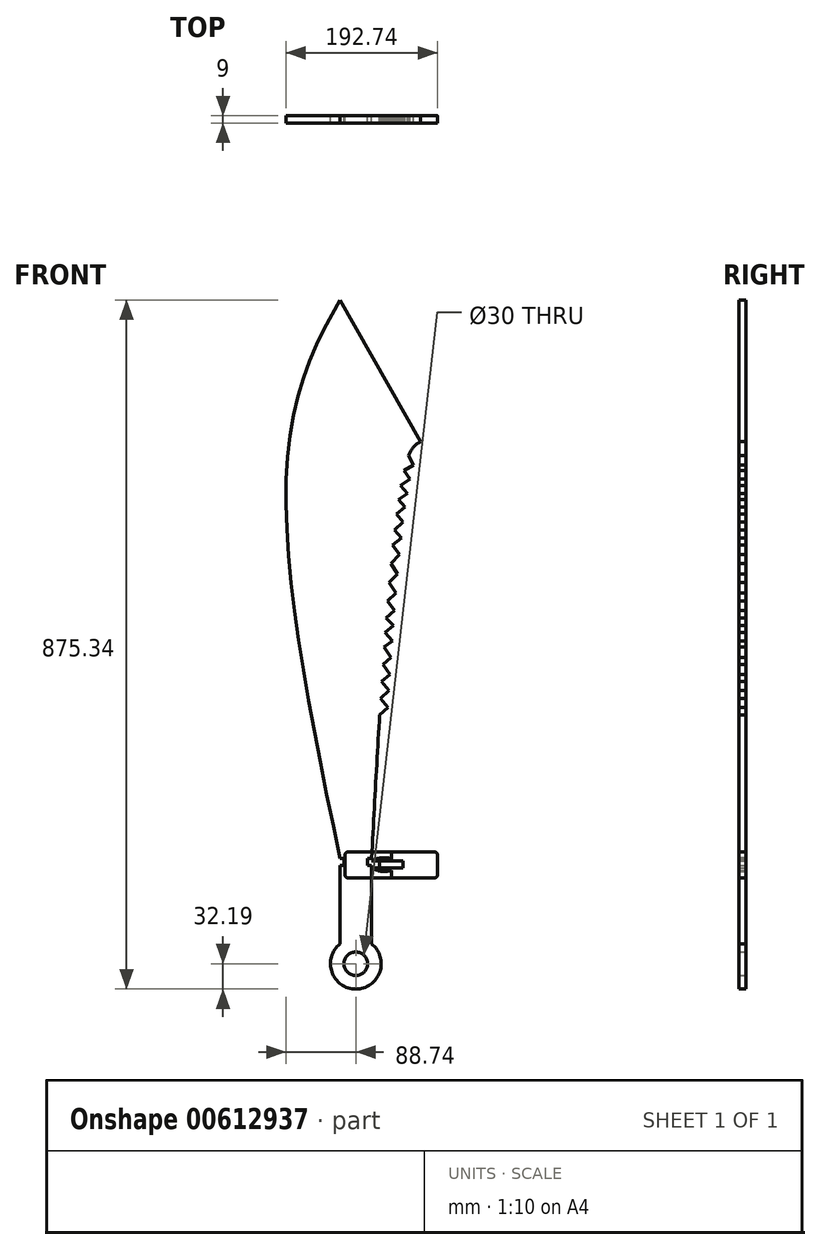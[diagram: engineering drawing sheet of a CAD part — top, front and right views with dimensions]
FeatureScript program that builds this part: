
annotation { "Feature Type Name" : "Feature", "Feature Type Description" : "" }
export const myFeature = defineFeature(function(context is Context, id is Id, definition is map)
    precondition{}
    {
        {
            var Q0;
            Q0=qCreatedBy(makeId("Front.planeOp"),FACE);
            var sketch = newSketch(context, id + "F0", { "sketchPlane" : qUnion([Q0])});
            skLineSegment(sketch, "E0.top", {"start": v(20, 49.92) * mm, "end": v(-20, 49.92) * mm});
            skLineSegment(sketch, "E0.left", {"start": v(20, -49.92) * mm, "end": v(20, 49.92) * mm});
            skLineSegment(sketch, "E0.right", {"start": v(-20, -49.92) * mm, "end": v(-20, 49.92) * mm});
            skPoint(sketch, "E0.middle", {"position": v(0, 0) * mm});
            skLineSegment(sketch, "E1", {"start": v(20, 49.92) * mm, "end": v(15, 49.92) * mm, "construction": true});
            skLineSegment(sketch, "E2", {"start": v(-20, 49.92) * mm, "end": v(-15, 49.92) * mm, "construction": true});
            skLineSegment(sketch, "E3", {"start": v(-15, 49.92) * mm, "end": v(-15, 58.92) * mm, "construction": true});
            skLineSegment(sketch, "E4", {"start": v(15, 58.92) * mm, "end": v(15, 49.92) * mm, "construction": true});
            skFitSpline(sketch, "E5", {"points": [v(20, 58.92) * mm, v(66.96, 570.52) * mm, v(82.11, 588.05) * mm], "startDerivative": vector(45.15, 820.54) * mm, "endDerivative": vector(88.4, 54.26) * mm});
            skLineSegment(sketch, "E6", {"start": v(82.11, 588.05) * mm, "end": v(-20, 768) * mm});
            skFitSpline(sketch, "E7", {"points": [v(-20, 58.92) * mm, v(-86.64, 570.52) * mm, v(-20, 768) * mm, v(22.37, 827.27) * mm], "startDerivative": vector(-243.66, 1152.7) * mm, "endDerivative": vector(43.6, -18.4) * mm});
            skLineSegment(sketch, "E8", {"start": v(20, 58.92) * mm, "end": v(15, 58.92) * mm});
            skLineSegment(sketch, "E9", {"start": v(15, 49.92) * mm, "end": v(15, 58.92) * mm});
            skLineSegment(sketch, "E10", {"start": v(-20, 58.92) * mm, "end": v(-15, 58.92) * mm});
            skLineSegment(sketch, "E11", {"start": v(-15, 49.92) * mm, "end": v(-15, 58.92) * mm});
            skPoint(sketch, "E12.visualSharp", {"position": v(20, -49.92) * mm});
            skLineSegment(sketch, "E12.filletArc", {"start": v(20, -49.92) * mm, "end": v(20, -49.92) * mm});
            skPoint(sketch, "E13.visualSharp", {"position": v(-20, -49.92) * mm});
            skLineSegment(sketch, "E13.filletArc", {"start": v(-20, -49.92) * mm, "end": v(-20, -49.92) * mm});
            skLineSegment(sketch, "E14", {"start": v(0, -49.92) * mm, "end": v(0, -75.15) * mm, "construction": true});
            skArc(sketch, "E15", {"start": v(-20, -49.92) * mm, "mid": v(0, -107.34) * mm, "end": v(20, -49.92) * mm});
            skCircle(sketch, "E16", {"center": v(0, -75.15) * mm, "radius": 15 * mm});
            skLineSegment(sketch, "E17", {"start": v(66.96, 570.52) * mm, "end": v(73.2, 558.15) * mm});
            skLineSegment(sketch, "E18", {"start": v(73.2, 558.15) * mm, "end": v(61, 551.35) * mm});
            skLineSegment(sketch, "E19", {"start": v(61, 551.35) * mm, "end": v(68.86, 540.72) * mm});
            skLineSegment(sketch, "E20", {"start": v(68.86, 540.72) * mm, "end": v(56.98, 532.25) * mm});
            skLineSegment(sketch, "E21", {"start": v(56.98, 532.25) * mm, "end": v(65.4, 522.25) * mm});
            skLineSegment(sketch, "E22", {"start": v(65.4, 522.25) * mm, "end": v(54, 514.42) * mm});
            skLineSegment(sketch, "E23", {"start": v(54, 514.42) * mm, "end": v(62.69, 504.73) * mm});
            skLineSegment(sketch, "E24", {"start": v(62.69, 504.73) * mm, "end": v(51.36, 495.86) * mm});
            skLineSegment(sketch, "E25", {"start": v(51.36, 495.86) * mm, "end": v(60.17, 485.9) * mm});
            skLineSegment(sketch, "E26", {"start": v(60.17, 485.9) * mm, "end": v(48.87, 475.9) * mm});
            skLineSegment(sketch, "E27", {"start": v(48.87, 475.9) * mm, "end": v(57.81, 465.9) * mm});
            skLineSegment(sketch, "E28", {"start": v(57.81, 465.9) * mm, "end": v(46.77, 457) * mm});
            skLineSegment(sketch, "E29", {"start": v(46.77, 457) * mm, "end": v(55.57, 444.65) * mm});
            skLineSegment(sketch, "E30", {"start": v(55.57, 444.65) * mm, "end": v(44.4, 433.34) * mm});
            skLineSegment(sketch, "E31", {"start": v(44.4, 433.34) * mm, "end": v(53.18, 419.7) * mm});
            skLineSegment(sketch, "E32", {"start": v(53.18, 419.7) * mm, "end": v(42.21, 409.4) * mm});
            skLineSegment(sketch, "E33", {"start": v(42.21, 409.4) * mm, "end": v(51.12, 396.02) * mm});
            skLineSegment(sketch, "E34", {"start": v(51.12, 396.02) * mm, "end": v(40.2, 385.4) * mm});
            skLineSegment(sketch, "E35", {"start": v(40.2, 385.4) * mm, "end": v(49.33, 373.87) * mm});
            skLineSegment(sketch, "E36", {"start": v(49.33, 373.87) * mm, "end": v(38.53, 364.07) * mm});
            skLineSegment(sketch, "E37", {"start": v(38.53, 364.07) * mm, "end": v(47.85, 354.5) * mm});
            skLineSegment(sketch, "E38", {"start": v(47.85, 354.5) * mm, "end": v(37.18, 345.88) * mm});
            skLineSegment(sketch, "E39", {"start": v(37.18, 345.88) * mm, "end": v(46.42, 334.84) * mm});
            skLineSegment(sketch, "E40", {"start": v(46.42, 334.84) * mm, "end": v(35.85, 327.14) * mm});
            skLineSegment(sketch, "E41", {"start": v(35.85, 327.14) * mm, "end": v(44.97, 313.9) * mm});
            skLineSegment(sketch, "E42", {"start": v(44.97, 313.9) * mm, "end": v(34.35, 305.24) * mm});
            skLineSegment(sketch, "E43", {"start": v(34.35, 305.24) * mm, "end": v(43.53, 292.29) * mm});
            skLineSegment(sketch, "E44", {"start": v(43.53, 292.29) * mm, "end": v(32.92, 283.37) * mm});
            skLineSegment(sketch, "E45", {"start": v(32.92, 283.37) * mm, "end": v(42.23, 272.02) * mm});
            skLineSegment(sketch, "E46", {"start": v(42.23, 272.02) * mm, "end": v(31.57, 262.05) * mm});
            skLineSegment(sketch, "E47", {"start": v(31.57, 262.05) * mm, "end": v(40.9, 250.72) * mm});
            skLineSegment(sketch, "E48", {"start": v(40.9, 250.72) * mm, "end": v(30.27, 240.75) * mm});
            skFitSpline(sketch, "E49.trimOffspring", {"points": [v(20, 68) * mm, v(66.96, 570.52) * mm, v(82.11, 588.05) * mm], "startDerivative": vector(45.15, 820.54) * mm, "endDerivative": vector(88.4, 54.26) * mm});
            skFitSpline(sketch, "E50", {"points": [v(0, 607.86) * mm, v(-16.19, 333.23) * mm], "startDerivative": vector(-237.44, -220.25) * mm, "endDerivative": vector(-48.57, -603.64) * mm});
            skArc(sketch, "E51.0.startCap", {"start": v(-10.44, 618.63) * mm, "mid": v(10.76, 617.86) * mm, "end": v(9.98, 596.66) * mm});
            skArc(sketch, "E51.0.endCap", {"start": v(-1.24, 332.03) * mm, "mid": v(-17.4, 318.28) * mm, "end": v(-31.14, 334.43) * mm});
            skFitSpline(sketch, "E51.0.left", {"points": [v(10.2, 596.86) * mm, v(5.48, 592.48) * mm, v(-2.63, 584.4) * mm, v(-9.76, 575.81) * mm, v(-13.88, 569.74) * mm, v(-16.27, 565.56) * mm, v(-18.05, 561.68) * mm, v(-19.32, 558.02) * mm, v(-20.18, 554.45) * mm, v(-20.68, 550.82) * mm, v(-20.86, 547) * mm, v(-20.72, 542.85) * mm, v(-20.27, 538.3) * mm, v(-19.24, 531.66) * mm, v(-17.23, 522.17) * mm, v(-13.94, 508.67) * mm, v(-10.18, 492.85) * mm, v(-6.38, 474.46) * mm, v(-2.96, 453.2) * mm, v(-0.32, 428.76) * mm, v(1.65, 391.47) * mm, v(0.83, 357.66) * mm, v(-1.24, 332.03) * mm]});
            skFitSpline(sketch, "E51.0.right", {"points": [v(-10.2, 618.86) * mm, v(-15.38, 614.05) * mm, v(-24.57, 604.93) * mm, v(-33.52, 594.21) * mm, v(-39.3, 585.75) * mm, v(-42.94, 579.39) * mm, v(-45.9, 572.98) * mm, v(-48.15, 566.5) * mm, v(-49.7, 560) * mm, v(-50.6, 553.52) * mm, v(-50.9, 547.08) * mm, v(-50.67, 540.72) * mm, v(-50.02, 534.4) * mm, v(-48.71, 525.97) * mm, v(-46.42, 515.26) * mm, v(-43.07, 501.52) * mm, v(-39.46, 486.3) * mm, v(-35.9, 469.03) * mm, v(-32.7, 449.23) * mm, v(-30.24, 426.4) * mm, v(-28.38, 391.32) * mm, v(-29.16, 359.1) * mm, v(-31.14, 334.43) * mm]});
            skSolve(sketch);
        }
        {
            var Q0;
            Q0 = qSketchRegion(id + "F0", true);
            extrude(context, id + "F1", {"entities" : qUnion([Q0]), "depth" : 9 * mm, "offsetDistance" : 25 * mm});
        }
        {
            var Q0;
            Q0=qCreatedBy(makeId("Front.planeOp"),FACE);
            var sketch = newSketch(context, id + "F2", { "sketchPlane" : qUnion([Q0])});
            skLineSegment(sketch, "E52.right", {"start": v(104, 55.36) * mm, "end": v(104, 46.36) * mm, "construction": true});
            skLineSegment(sketch, "E53.right", {"start": v(45, 58.1) * mm, "end": v(45, 58.1) * mm});
            skFitSpline(sketch, "E54", {"points": [v(15, 53.1) * mm, v(30, 59.03) * mm, v(45, 58.1) * mm], "startDerivative": vector(29.6, 13.81) * mm, "endDerivative": vector(30.4, -9.38) * mm});
            skFitSpline(sketch, "E55.MirrorCS", {"points": [v(15, 48.6) * mm, v(30, 42.68) * mm, v(45, 43.6) * mm], "startDerivative": vector(29.6, -13.81) * mm, "endDerivative": vector(30.4, 9.38) * mm});
            skLineSegment(sketch, "E56", {"start": v(45, 67.18) * mm, "end": v(99, 67.18) * mm});
            skLineSegment(sketch, "E57", {"start": v(104, 62.18) * mm, "end": v(104, 43.6) * mm});
            skLineSegment(sketch, "E58", {"start": v(104, 38.6) * mm, "end": v(104, 43.6) * mm});
            skLineSegment(sketch, "E59", {"start": v(45, 43.6) * mm, "end": v(45, 33.6) * mm});
            skLineSegment(sketch, "E60", {"start": v(45, 33.6) * mm, "end": v(99, 33.6) * mm});
            skLineSegment(sketch, "E61", {"start": v(45, 58.1) * mm, "end": v(45, 67.18) * mm});
            skPoint(sketch, "E62.visualSharp", {"position": v(104, 67.18) * mm});
            skArc(sketch, "E62.filletArc", {"start": v(104, 62.18) * mm, "mid": v(102.54, 65.72) * mm, "end": v(99, 67.18) * mm});
            skPoint(sketch, "E63.visualSharp", {"position": v(104, 33.6) * mm});
            skArc(sketch, "E63.filletArc", {"start": v(99, 33.6) * mm, "mid": v(102.54, 35.07) * mm, "end": v(104, 38.6) * mm});
            skPoint(sketch, "E64.MirrorP", {"position": v(-14, 67.18) * mm});
            skLineSegment(sketch, "E65.MirrorCS", {"start": v(-14, 55.36) * mm, "end": v(-14, 46.36) * mm, "construction": true});
            skPoint(sketch, "E66.MirrorP", {"position": v(-14, 33.6) * mm});
            skLineSegment(sketch, "E67.MirrorCS", {"start": v(-14, 38.6) * mm, "end": v(-14, 43.6) * mm});
            skArc(sketch, "E68.MirrorCS", {"start": v(-14, 62.18) * mm, "mid": v(-12.53, 65.72) * mm, "end": v(-9, 67.18) * mm});
            skLineSegment(sketch, "E69.MirrorCS", {"start": v(45, 33.6) * mm, "end": v(-9, 33.6) * mm});
            skLineSegment(sketch, "E70.MirrorCS", {"start": v(-14, 62.18) * mm, "end": v(-14, 43.6) * mm});
            skLineSegment(sketch, "E71.MirrorCS", {"start": v(45, 67.18) * mm, "end": v(-9, 67.18) * mm});
            skArc(sketch, "E72.MirrorCS", {"start": v(-9, 33.6) * mm, "mid": v(-12.53, 35.07) * mm, "end": v(-14, 38.6) * mm});
            skLineSegment(sketch, "E73.bottom", {"start": v(60.02, 46.35) * mm, "end": v(29.98, 46.35) * mm});
            skLineSegment(sketch, "E73.top", {"start": v(60.02, 55.36) * mm, "end": v(29.98, 55.36) * mm});
            skLineSegment(sketch, "E73.left", {"start": v(60.02, 46.35) * mm, "end": v(60.02, 55.36) * mm});
            skLineSegment(sketch, "E74", {"start": v(29.98, 55.36) * mm, "end": v(19.8, 55.36) * mm});
            skLineSegment(sketch, "E75", {"start": v(19.8, 46.35) * mm, "end": v(29.98, 46.35) * mm});
            skLineSegment(sketch, "E76", {"start": v(45, 58.1) * mm, "end": v(45, 43.6) * mm, "construction": true});
            skLineSegment(sketch, "E77.right", {"start": v(29.98, 46.35) * mm, "end": v(29.98, 55.36) * mm});
            skPoint(sketch, "E77.middle", {"position": v(45, 50.86) * mm});
            skSolve(sketch);
        }
        {
            var Q0;
            Q0=makeQuery(id+"F2.imprint","IMPRINT",FACE,{"disambiguationData":[TD([[makeQuery(id+"F2.imprint","IMPRINT",EDGE,{"derivedFrom":sQuery(id+"F2.wireOp",EDGE,"E56")}),-1.0]])]});
            var Q1;
            {var subQ1=sQuery(id+"F2.wireOp",EDGE,"07f323f2-1cfc-49b7-a9e3-ff4e74a766695.MirrorCS");Q1=makeQuery(id+"F2.imprint","IMPRINT",FACE,{"disambiguationData":[TD([[makeQuery(id+"F2.imprint","IMPRINT",EDGE,{"derivedFrom":subQ1}),-1.0]])]});}
            var Q2;
            {var subQ6=sQuery(id+"F2.wireOp",EDGE,"07f323f2-1cfc-49b7-a9e3-ff4e74a766693.MirrorCS");Q2=makeQuery(id+"F2.imprint","IMPRINT",FACE,{"disambiguationData":[TD([[makeQuery(id+"F2.imprint","IMPRINT",EDGE,{"derivedFrom":subQ6}),-1.0]])]});}
            var Q3;
            {var subQ0=sQuery(id+"F2.wireOp",EDGE,"07f323f2-1cfc-49b7-a9e3-ff4e74a7666912.MirrorCS");var subQ5=sQuery(id+"F2.wireOp",EDGE,"xr9Mq38u-gtu0-ojOd-W7Qr-ZrPNSoZhxPpX.bottom");var subQ6=makeQuery(id+"F2.imprint","INTERSECT",VERTEX,{"derivedFrom":[subQ0,subQ5]});Q3=makeQuery(id+"F2.imprint","IMPRINT",FACE,{"disambiguationData":[TD([[makeQuery(id+"F2.imprint","IMPRINT",EDGE,{"disambiguationData":[TD([[subQ6,-1.0]])],"derivedFrom":subQ5}),1.0]])]});}
            extrude(context, id + "F3", {"entities" : qUnion([Q0, Q1, Q2, Q3]), "depth" : 9 * mm, "offsetDistance" : 25 * mm});
        }
        {
            var Q0;
            {var subQ0=sQuery(id+"F2.wireOp",EDGE,"E61");Q0=makeQuery(id+"F2.imprint","IMPRINT",FACE,{"disambiguationData":[TD([[makeQuery(id+"F2.imprint","IMPRINT",EDGE,{"derivedFrom":subQ0}),1.0]])]});}
            extrude(context, id + "F4", {"entities" : qUnion([Q0]), "depth" : 9 * mm, "offsetDistance" : 25 * mm});
        }
    });
